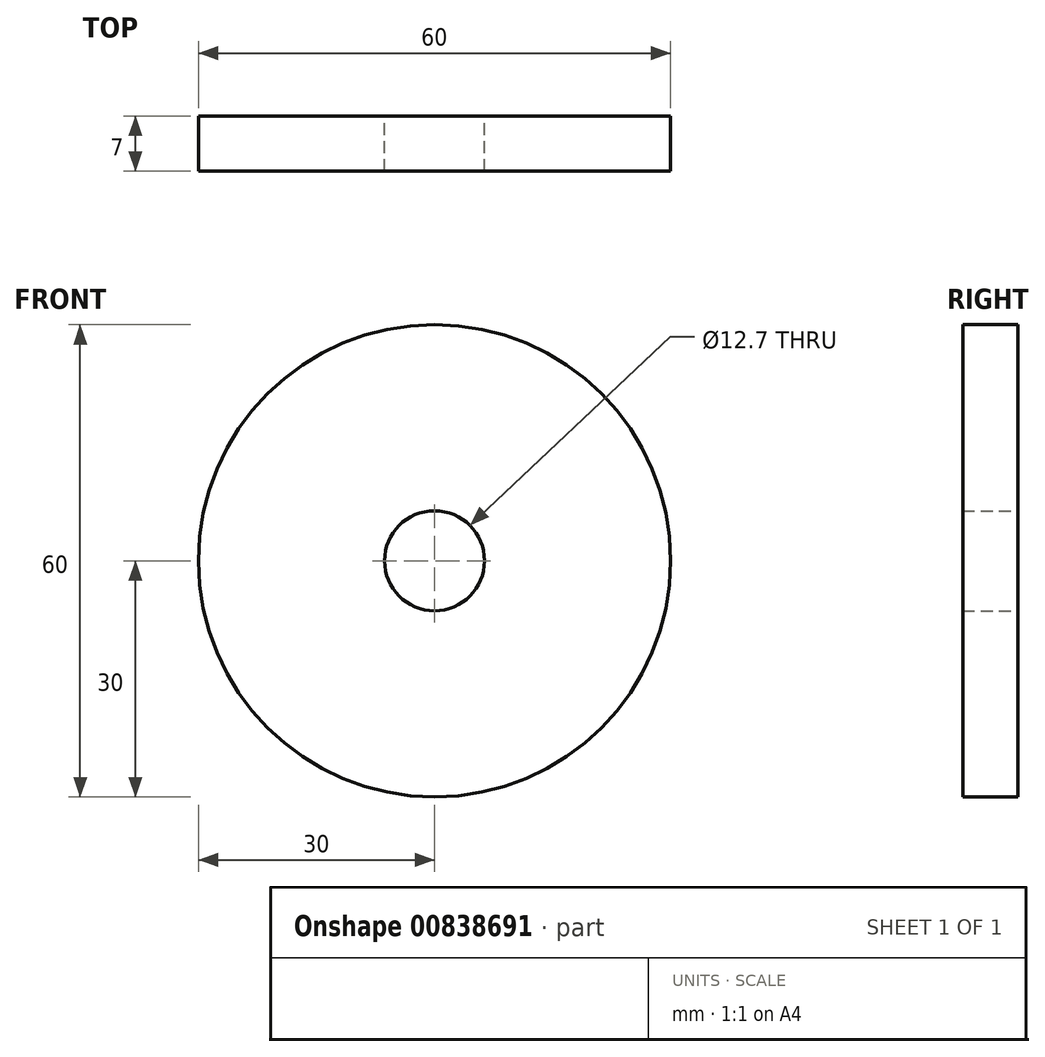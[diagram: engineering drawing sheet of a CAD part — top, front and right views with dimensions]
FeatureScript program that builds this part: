
annotation { "Feature Type Name" : "Feature", "Feature Type Description" : "" }
export const myFeature = defineFeature(function(context is Context, id is Id, definition is map)
    precondition{}
    {
        {
            var Q0;
            Q0=qCreatedBy(makeId("Front.planeOp"),FACE);
            var sketch = newSketch(context, id + "F0", { "sketchPlane" : qUnion([Q0])});
            skCircle(sketch, "E0", {"center": v(0, 0) * mm, "radius": 30 * mm});
            skSolve(sketch);
        }
        {
            var Q0;
            Q0=makeQuery(id+"F0.imprint","IMPRINT",FACE,{"disambiguationData":[TD([[makeQuery(id+"F0.imprint","IMPRINT",EDGE,{"derivedFrom":sQuery(id+"F0.wireOp",EDGE,"E0")}),1.0]])]});
            extrude(context, id + "F1", {"entities" : qUnion([Q0]), "depth" : 7 * mm, "offsetDistance" : 25 * mm});
        }
        {
            var Q0;
            Q0=makeQuery(id+"F1.opExtrude","CAP_FACE",FACE,{"disambiguationData":[OSD([sQuery(id+"F0.wireOp",EDGE,"E0")])],"isStart":true});
            var sketch = newSketch(context, id + "F2", { "sketchPlane" : qUnion([Q0])});
            skCircle(sketch, "E1", {"center": v(0, 0) * mm, "radius": 6.35 * mm});
            skSolve(sketch);
        }
        {
            var Q0;
            Q0=makeQuery(id+"F2.imprint","IMPRINT",FACE,{"disambiguationData":[TD([[makeQuery(id+"F2.imprint","IMPRINT",EDGE,{"derivedFrom":sQuery(id+"F2.wireOp",EDGE,"E1")}),1.0]])]});
            extrude(context, id + "F3", {"entities" : qUnion([Q0]), "operationType" : NewBodyOperationType.REMOVE, "endBound" : BoundingType.THROUGH_ALL, "oppositeDirection" : true, "depth" : 25 * mm, "offsetDistance" : 25 * mm});
        }
    });
